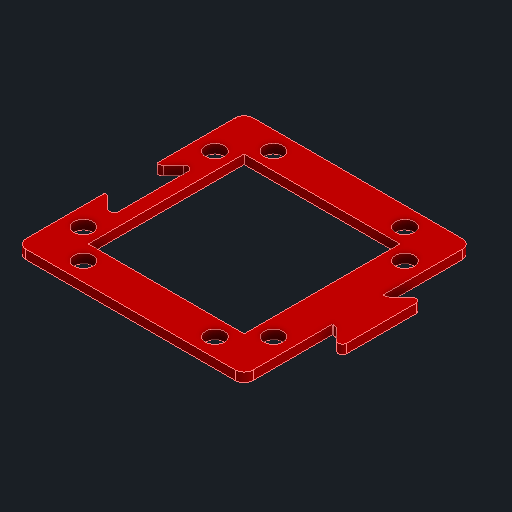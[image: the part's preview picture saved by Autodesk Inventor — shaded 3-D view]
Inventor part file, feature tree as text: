
AUTODESK INVENTOR PART (.ipt)
format: ipt  version: 2023.4 (Build 274418000, 418)  size: 388,096 bytes
history: native  units: mm
features: reference x9, extrude x3, other x3, sketch x2, fillet x1, projected_geometry x1
ambient origin geometry x8: Origin, YZ Plane, XZ Plane, XY Plane, X Axis, Y Axis, Z Axis, Center Point
bodies: Solid1 (feature_tree)
feature tree (19):
  extrude  "Extrusion1"  Depth=2.0mm TaperAngle=0.0deg
  sketch  "Sketch2"  dims[d16=10.0mm d17=0.0mm d18=0.25mm d19=20.0mm d20=10.0mm d21=45.0deg d22=1.0mm d23=1.5mm d24=1.0mm d25=0.075mm d28=15.171573mm d29=2.87868mm d30=2.87868mm d31=20.0mm d32=10.0mm d33=45.0deg d34=1.0mm d35=1.5mm d36=1.0mm d37=0.075mm d38=15.171573mm d39=2.87868mm d40=2.87868mm d41=0.25mm d42=0.0mm d43=40.0mm d45=360.0deg]
  extrude  "Extrusion2"  Depth=0.25mm
  extrude  "Extrusion3"  Depth=0.25mm
  fillet  "Fillet1"  Radius=2.87868mm
  sketch  "Sketch1"  dims[d0=2.0mm d1=0.0mm d14=2.0mm d15=0.0mm]
  reference  "Reference1"
  reference  "Reference2"
  reference  "Reference3"
  reference  "Reference4"
  reference  "Reference5"
  reference  "Reference6"
  reference  "Reference7"
  reference  "Reference8"
  reference  "Reference9"
  projected_geometry  "Projected Loop2"
  other  "<path>\Projects\Project Protocube\Protocube\CAD, STL, OBJ Files\1 CAD\Cube 1x1 V5.iam"
  other  "Cube 1x1 V5.iam"
  other  "Cube 1x1 Top V5:1"
note: 1 file-system path scrubbed to <path> (originals preserved in map.json)
